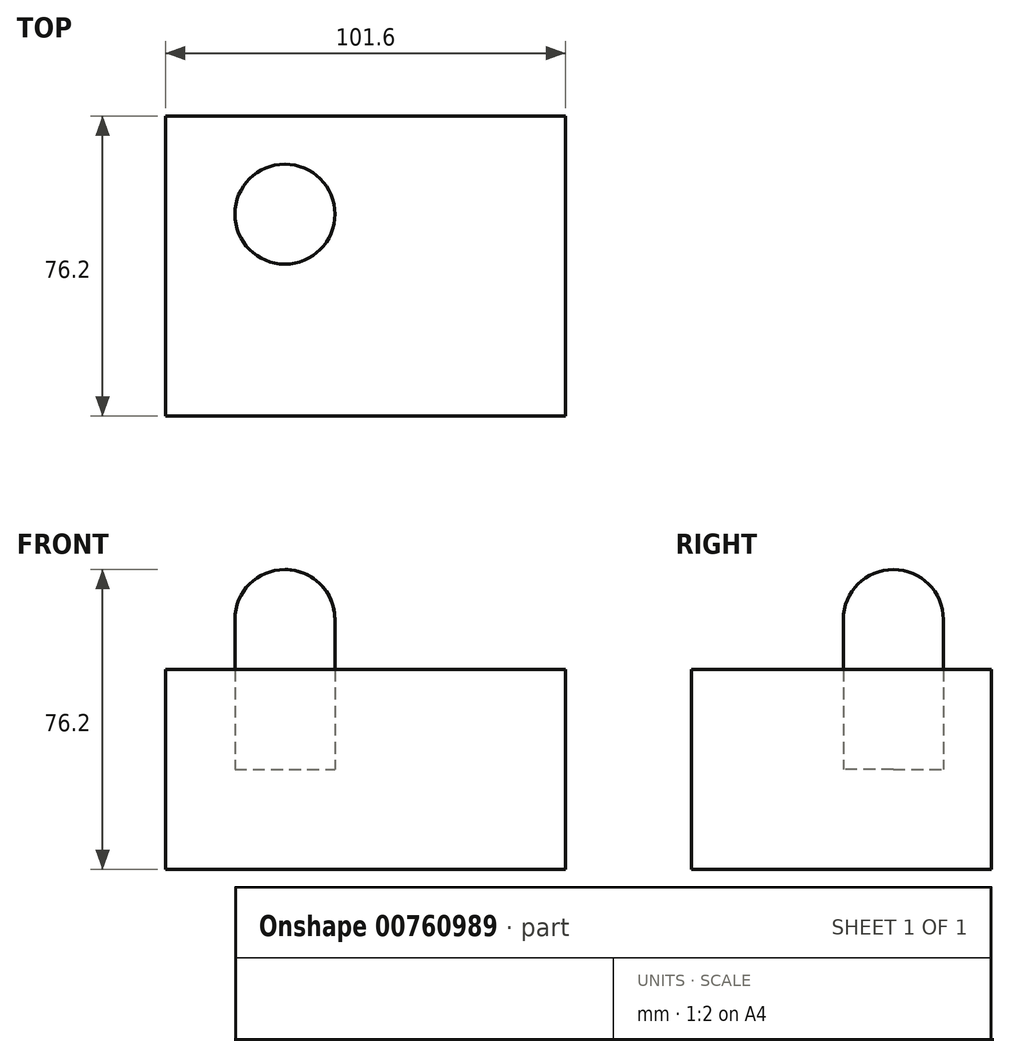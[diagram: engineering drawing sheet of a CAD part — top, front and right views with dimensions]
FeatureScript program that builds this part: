
annotation { "Feature Type Name" : "Feature", "Feature Type Description" : "" }
export const myFeature = defineFeature(function(context is Context, id is Id, definition is map)
    precondition{}
    {
        {
            var Q0;
            Q0=qCreatedBy(makeId("Top.planeOp"),FACE);
            var sketch = newSketch(context, id + "F0", { "sketchPlane" : qUnion([Q0])});
            skLineSegment(sketch, "E0.bottom", {"start": v(-43.7, 30.34) * mm, "end": v(57.9, 30.34) * mm});
            skLineSegment(sketch, "E0.top", {"start": v(-43.7, -45.86) * mm, "end": v(57.9, -45.86) * mm});
            skLineSegment(sketch, "E0.left", {"start": v(-43.7, 30.34) * mm, "end": v(-43.7, -45.86) * mm});
            skLineSegment(sketch, "E0.right", {"start": v(57.9, 30.34) * mm, "end": v(57.9, -45.86) * mm});
            skSolve(sketch);
        }
        {
            var Q0;
            Q0=makeQuery(id+"F0.imprint","IMPRINT",FACE,{"disambiguationData":[TD([[makeQuery(id+"F0.imprint","IMPRINT",EDGE,{"derivedFrom":sQuery(id+"F0.wireOp",EDGE,"E0.bottom")}),-1.0]])]});
            extrude(context, id + "F1", {"entities" : qUnion([Q0]), "depth" : 50.8 * mm, "offsetDistance" : 25.4 * mm});
        }
        {
            var Q0;
            Q0=makeQuery(id+"F1.opExtrude","CAP_FACE",FACE,{"disambiguationData":[OSD([sQuery(id+"F0.wireOp",EDGE,"E0.bottom"),sQuery(id+"F0.wireOp",EDGE,"E0.top"),sQuery(id+"F0.wireOp",EDGE,"E0.left"),sQuery(id+"F0.wireOp",EDGE,"E0.right")])],"isStart":false});
            var sketch = newSketch(context, id + "F2", { "sketchPlane" : qUnion([Q0])});
            skCircle(sketch, "E1", {"center": v(-13.39, 5.42) * mm, "radius": 12.7 * mm});
            skSolve(sketch);
        }
        {
            var Q0;
            Q0=makeQuery(id+"F2.imprint","IMPRINT",FACE,{"disambiguationData":[TD([[makeQuery(id+"F2.imprint","IMPRINT",EDGE,{"derivedFrom":sQuery(id+"F2.wireOp",EDGE,"E1")}),1.0]])]});
            extrude(context, id + "F3", {"entities" : qUnion([Q0]), "depth" : 25.4 * mm, "offsetDistance" : 25.4 * mm, "hasSecondDirection" : true, "secondDirectionOppositeDirection" : true, "secondDirectionDepth" : 25.4 * mm});
        }
        {
            var Q0;
            Q0=makeQuery(id+"F3.opExtrude","CAP_FACE",FACE,{"disambiguationData":[OSD([sQuery(id+"F2.wireOp",EDGE,"E1")])],"isStart":false});
            fillet(context, id + "F4", {"entities" : qUnion([Q0]), "radius" : 12.7 * mm, "tangentPropagation" : true, "allowEdgeOverflow" : false});
        }
    });
